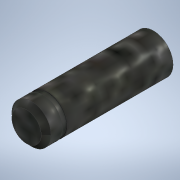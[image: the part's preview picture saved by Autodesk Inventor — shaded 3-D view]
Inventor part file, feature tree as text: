
AUTODESK INVENTOR PART (.ipt)
format: ipt  version: 2021 (Build 250183000, 183)  size: 123,904 bytes
history: native  units: mm
features: extrude x3, sketch x3, chamfer x1
ambient origin geometry x8: Origin, YZ Plane, XZ Plane, XY Plane, X Axis, Y Axis, Z Axis, Center Point
bodies: Solid1 (feature_tree)
feature tree (7):
  extrude  "Extrusion1"  Depth=10.8mm TaperAngle=0.0deg
  extrude  "Extrusion2"  Depth=0.5mm TaperAngle=0.0deg
  extrude  "Extrusion3"  Depth=0.5mm TaperAngle=45.0deg
  chamfer  "Chamfer1"  [1 undecoded]
  sketch  "Sketch1"  dims[d0=4.0mm d1=10.8mm d2=0.0mm]
  sketch  "Sketch2"  dims[d3=3.8mm d4=0.5mm d5=0.0mm]
  sketch  "Sketch3"  dims[d6=1.65mm d7=0.0mm d8=0.5mm d9=2.0mm d10=45.0deg]
note: 1 required parameter value undecoded (feature->parameter linkage not recoverable at this tier; creation-order binding heuristic only, values carry confidence <= 0.55)
